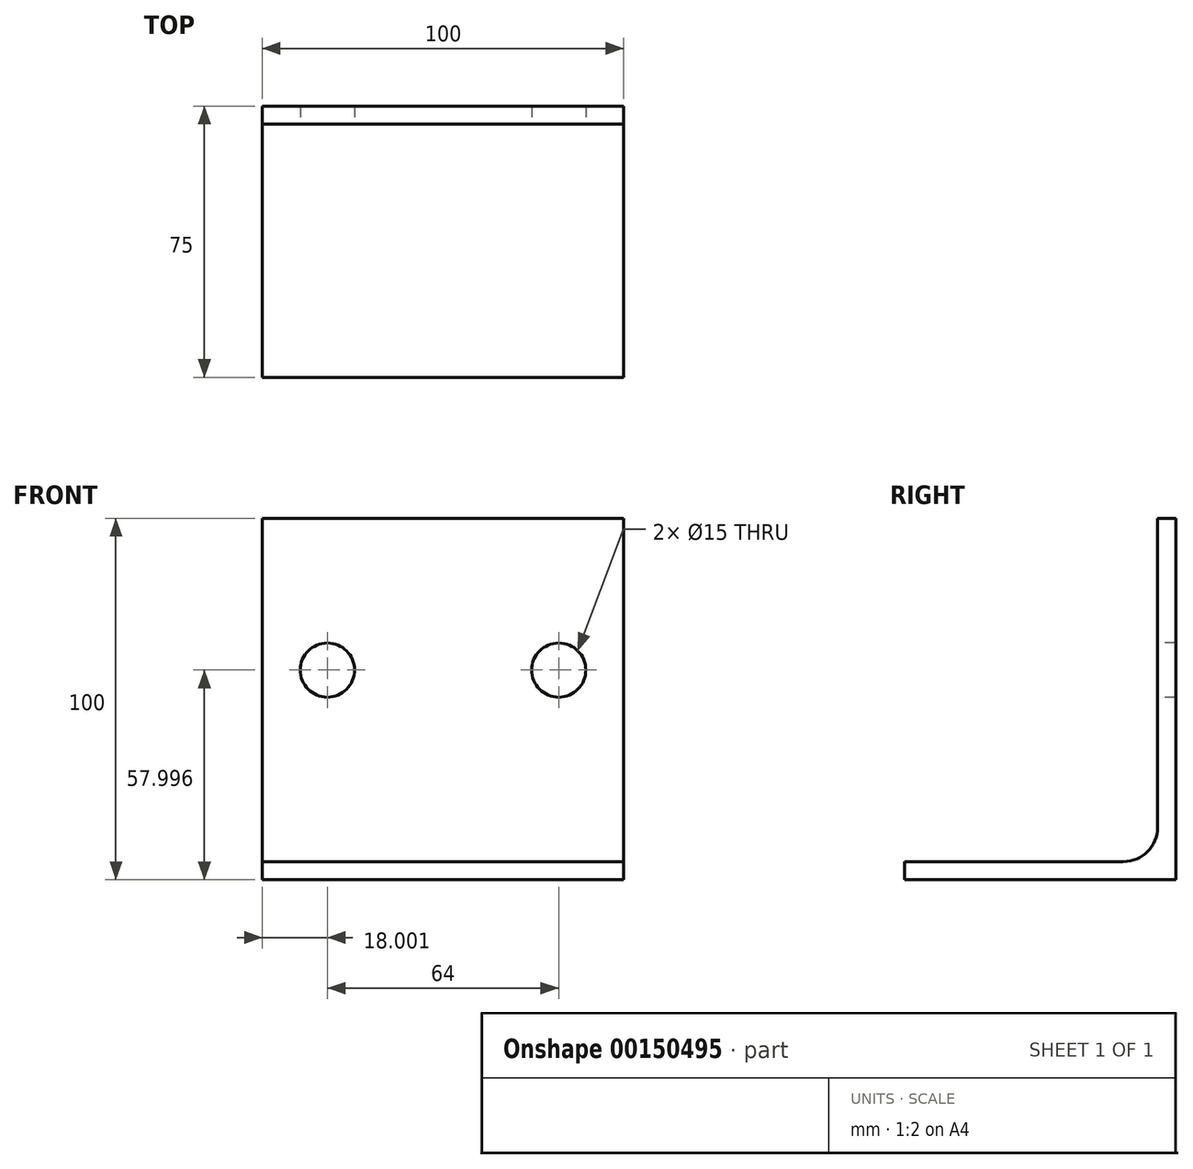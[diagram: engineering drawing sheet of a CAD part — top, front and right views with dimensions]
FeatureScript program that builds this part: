
annotation { "Feature Type Name" : "Feature", "Feature Type Description" : "" }
export const myFeature = defineFeature(function(context is Context, id is Id, definition is map)
    precondition{}
    {
        {
            var Q0;
            Q0=qCreatedBy(makeId("Front.planeOp"),FACE);
            var sketch = newSketch(context, id + "F0", { "sketchPlane" : qUnion([Q0])});
            skLineSegment(sketch, "E0.bottom", {"start": v(-61.64, 77.7) * mm, "end": v(38.36, 77.7) * mm});
            skLineSegment(sketch, "E0.top", {"start": v(-61.64, -22.3) * mm, "end": v(38.36, -22.3) * mm});
            skLineSegment(sketch, "E0.left", {"start": v(-61.64, 77.7) * mm, "end": v(-61.64, -22.3) * mm});
            skLineSegment(sketch, "E0.right", {"start": v(38.36, 77.7) * mm, "end": v(38.36, -22.3) * mm});
            skLineSegment(sketch, "E1.top", {"start": v(-61.64, -17.3) * mm, "end": v(38.36, -17.3) * mm});
            skLineSegment(sketch, "E1.left", {"start": v(-61.64, -22.3) * mm, "end": v(-61.64, -17.3) * mm});
            skLineSegment(sketch, "E1.right", {"start": v(38.36, -22.3) * mm, "end": v(38.36, -17.3) * mm});
            skSolve(sketch);
        }
        {
            var Q0;
            Q0=makeQuery(id+"F0.imprint","IMPRINT",FACE,{"disambiguationData":[TD([[makeQuery(id+"F0.imprint","IMPRINT",EDGE,{"derivedFrom":sQuery(id+"F0.wireOp",EDGE,"E0.top")}),1.0]])]});
            extrude(context, id + "F1", {"entities" : qUnion([Q0]), "depth" : 75 * mm});
        }
        {
            var Q0;
            Q0 = qSketchRegion(id + "F0", true);
            extrude(context, id + "F2", {"entities" : qUnion([Q0]), "operationType" : NewBodyOperationType.ADD, "depth" : 5 * mm});
        }
        {
            var Q0;
            Q0=makeQuery(id+"F2.boolean.opBoolean","INTERSECT",EDGE,{"derivedFrom":[makeQuery(id+"F1.opExtrude","SWEPT_FACE",FACE,{"disambiguationData":[OSD([sQuery(id+"F0.wireOp",EDGE,"E1.top")])]}),makeQuery(id+"F2.opExtrude","CAP_FACE",FACE,{"disambiguationData":[OSD([sQuery(id+"F0.wireOp",EDGE,"E0.bottom"),sQuery(id+"F0.wireOp",EDGE,"E0.left"),sQuery(id+"F0.wireOp",EDGE,"E0.right"),sQuery(id+"F0.wireOp",EDGE,"E0.top"),sQuery(id+"F0.wireOp",EDGE,"E1.left"),sQuery(id+"F0.wireOp",EDGE,"E1.right")])],"isStart":false})]});
            fillet(context, id + "F3", {"entities" : qUnion([Q0]), "radius" : 9.5 * mm, "tangentPropagation" : true, "allowEdgeOverflow" : false});
        }
        {
            var Q0;
            Q0=makeQuery(id+"F2.opExtrude","CAP_FACE",FACE,{"disambiguationData":[OSD([sQuery(id+"F0.wireOp",EDGE,"E0.bottom"),sQuery(id+"F0.wireOp",EDGE,"E0.left"),sQuery(id+"F0.wireOp",EDGE,"E0.right"),sQuery(id+"F0.wireOp",EDGE,"E0.top"),sQuery(id+"F0.wireOp",EDGE,"E1.left"),sQuery(id+"F0.wireOp",EDGE,"E1.right")])],"isStart":false});
            var sketch = newSketch(context, id + "F4", { "sketchPlane" : qUnion([Q0])});
            skCircle(sketch, "E2", {"center": v(-43.64, 35.7) * mm, "radius": 7.5 * mm});
            skCircle(sketch, "E3", {"center": v(20.36, 35.7) * mm, "radius": 7.5 * mm});
            skSolve(sketch);
        }
        {
            var Q0;
            Q0=makeQuery(id+"F4.imprint","IMPRINT",FACE,{"disambiguationData":[TD([[makeQuery(id+"F4.imprint","IMPRINT",EDGE,{"derivedFrom":sQuery(id+"F4.wireOp",EDGE,"E3")}),1.0]])]});
            var Q1;
            Q1=makeQuery(id+"F4.imprint","IMPRINT",FACE,{"disambiguationData":[TD([[makeQuery(id+"F4.imprint","IMPRINT",EDGE,{"derivedFrom":sQuery(id+"F4.wireOp",EDGE,"E2")}),1.0]])]});
            extrude(context, id + "F5", {"entities" : qUnion([Q0, Q1]), "operationType" : NewBodyOperationType.REMOVE, "endBound" : BoundingType.THROUGH_ALL, "oppositeDirection" : true, "depth" : 25 * mm});
        }
    });
